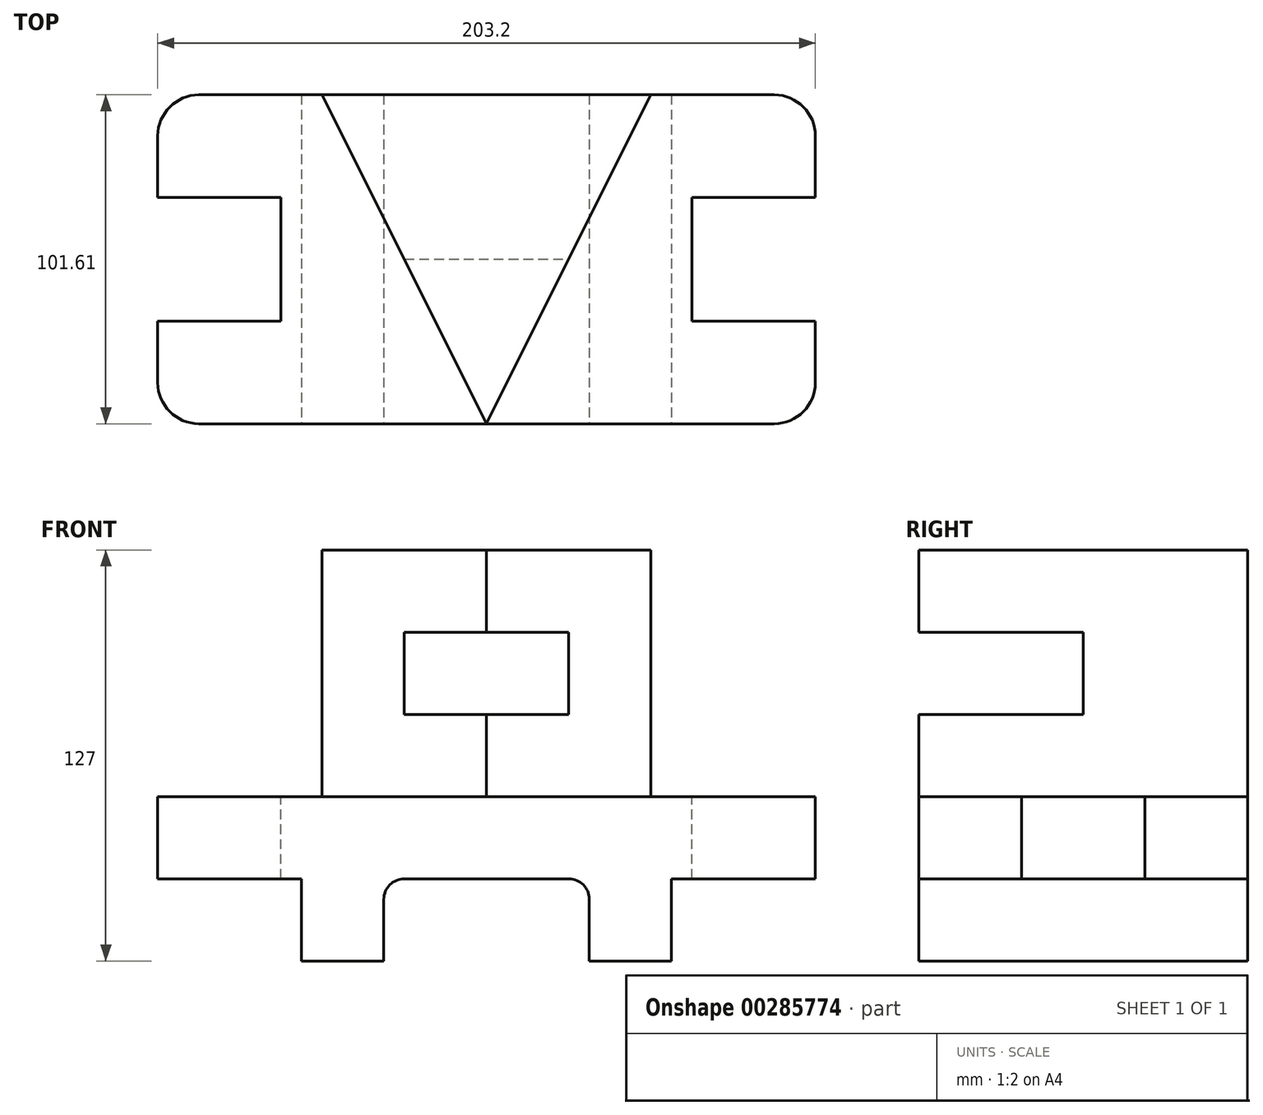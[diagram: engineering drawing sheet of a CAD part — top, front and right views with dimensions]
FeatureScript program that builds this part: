
annotation { "Feature Type Name" : "Feature", "Feature Type Description" : "" }
export const myFeature = defineFeature(function(context is Context, id is Id, definition is map)
    precondition{}
    {
        {
            var Q0;
            Q0=qCreatedBy(makeId("Top.planeOp"),FACE);
            var sketch = newSketch(context, id + "F0", { "sketchPlane" : qUnion([Q0])});
            skLineSegment(sketch, "E0", {"start": v(-50.8, 0) * mm, "end": v(50.8, 0) * mm});
            skLineSegment(sketch, "E1", {"start": v(0, 0) * mm, "end": v(0, -101.6) * mm, "construction": true});
            skLineSegment(sketch, "E2", {"start": v(50.8, 0) * mm, "end": v(0, -101.6) * mm});
            skLineSegment(sketch, "E3", {"start": v(-50.8, 0) * mm, "end": v(0, -101.6) * mm});
            skLineSegment(sketch, "E4", {"start": v(-25.4, -50.8) * mm, "end": v(25.4, -50.8) * mm});
            skSolve(sketch);
        }
        {
            var Q0;
            {var subQ3=sQuery(id+"F0.wireOp",EDGE,"E4");Q0=makeQuery(id+"F0.imprint","IMPRINT",FACE,{"disambiguationData":[TD([[makeQuery(id+"F0.imprint","IMPRINT",EDGE,{"derivedFrom":subQ3}),-1.0]])]});}
            var Q1;
            {var subQ0=sQuery(id+"F0.wireOp",EDGE,"E0");Q1=makeQuery(id+"F0.imprint","IMPRINT",FACE,{"disambiguationData":[TD([[makeQuery(id+"F0.imprint","IMPRINT",EDGE,{"derivedFrom":subQ0}),-1.0]])]});}
            extrude(context, id + "F1", {"entities" : qUnion([Q0, Q1]), "endBound" : BoundingType.SYMMETRIC, "depth" : 76.2 * mm});
        }
        {
            var Q0;
            {var subQ3=sQuery(id+"F0.wireOp",EDGE,"E4");Q0=makeQuery(id+"F0.imprint","IMPRINT",FACE,{"disambiguationData":[TD([[makeQuery(id+"F0.imprint","IMPRINT",EDGE,{"derivedFrom":subQ3}),-1.0]])]});}
            extrude(context, id + "F2", {"entities" : qUnion([Q0]), "operationType" : NewBodyOperationType.REMOVE, "endBound" : BoundingType.SYMMETRIC, "oppositeDirection" : true, "depth" : 25.4 * mm});
        }
        {
            var Q0;
            Q0=makeQuery(id+"F1.opExtrude","CAP_FACE",FACE,{"disambiguationData":[OSD([sQuery(id+"F0.wireOp",EDGE,"E0"),sQuery(id+"F0.wireOp",EDGE,"E2"),sQuery(id+"F0.wireOp",EDGE,"E3")])],"isStart":true});
            var sketch = newSketch(context, id + "F3", { "sketchPlane" : qUnion([Q0])});
            skLineSegment(sketch, "E5", {"start": v(-101.6, 0) * mm, "end": v(101.6, 0) * mm});
            skPoint(sketch, "E5.startSnap0", {"position": v(0, 0) * mm});
            skLineSegment(sketch, "E6", {"start": v(-101.6, 0) * mm, "end": v(-101.6, 101.6) * mm});
            skLineSegment(sketch, "E7", {"start": v(-101.6, 101.6) * mm, "end": v(101.6, 101.6) * mm});
            skLineSegment(sketch, "E8", {"start": v(101.6, 101.6) * mm, "end": v(101.6, 0) * mm});
            skArc(sketch, "E9", {"start": v(-88.9, 101.6) * mm, "mid": v(-97.88, 97.89) * mm, "end": v(-101.6, 88.9) * mm});
            skArc(sketch, "E10", {"start": v(101.6, 88.9) * mm, "mid": v(97.88, 97.89) * mm, "end": v(88.9, 101.6) * mm});
            skArc(sketch, "E11", {"start": v(88.9, 0) * mm, "mid": v(97.88, 3.72) * mm, "end": v(101.6, 12.7) * mm});
            skArc(sketch, "E12", {"start": v(-101.6, 12.7) * mm, "mid": v(-97.88, 3.72) * mm, "end": v(-88.9, 0) * mm});
            skLineSegment(sketch, "E13", {"start": v(-101.6, 31.75) * mm, "end": v(-63.5, 31.75) * mm});
            skLineSegment(sketch, "E14", {"start": v(-63.5, 31.75) * mm, "end": v(-63.5, 69.86) * mm});
            skLineSegment(sketch, "E15", {"start": v(-63.5, 69.86) * mm, "end": v(-101.6, 69.86) * mm});
            skLineSegment(sketch, "E16", {"start": v(101.6, 69.86) * mm, "end": v(63.5, 69.86) * mm});
            skLineSegment(sketch, "E17", {"start": v(63.5, 69.86) * mm, "end": v(63.5, 31.75) * mm});
            skLineSegment(sketch, "E18", {"start": v(63.5, 31.75) * mm, "end": v(101.6, 31.75) * mm});
            skSolve(sketch);
        }
        {
            var Q0;
            {var subQ2=makeQuery(id+"F1.opExtrude","CAP_EDGE",EDGE,{"disambiguationData":[OSD([sQuery(id+"F0.wireOp",EDGE,"E2")])],"isStart":true});Q0=makeQuery(id+"F3.imprint","IMPRINT",FACE,{"disambiguationData":[TD([[makeQuery(id+"F3.imprint","IMPRINT",EDGE,{"derivedFrom":subQ2}),1.0]])]});}
            var Q1;
            {var subQ1=sQuery(id+"F3.wireOp",EDGE,"E9");Q1=makeQuery(id+"F3.imprint","IMPRINT",FACE,{"disambiguationData":[TD([[makeQuery(id+"F3.imprint","IMPRINT",EDGE,{"derivedFrom":subQ1}),1.0]])]});}
            extrude(context, id + "F4", {"entities" : qUnion([Q0, Q1]), "operationType" : NewBodyOperationType.ADD, "depth" : 25.4 * mm});
        }
        {
            var Q0;
            Q0=makeQuery(id+"F4.opExtrude","SWEPT_FACE",FACE,{"disambiguationData":[OSD([sQuery(id+"F3.wireOp",EDGE,"E7")])]});
            var sketch = newSketch(context, id + "F5", { "sketchPlane" : qUnion([Q0])});
            skLineSegment(sketch, "E19", {"start": v(-57.15, -63.5) * mm, "end": v(-57.15, -88.9) * mm});
            skLineSegment(sketch, "E20", {"start": v(-57.15, -88.9) * mm, "end": v(-31.75, -88.9) * mm});
            skLineSegment(sketch, "E21", {"start": v(-31.75, -88.9) * mm, "end": v(-31.75, -63.5) * mm});
            skLineSegment(sketch, "E22", {"start": v(31.75, -63.5) * mm, "end": v(31.75, -88.9) * mm});
            skLineSegment(sketch, "E23", {"start": v(31.75, -88.9) * mm, "end": v(57.15, -88.9) * mm});
            skLineSegment(sketch, "E24", {"start": v(57.15, -88.9) * mm, "end": v(57.15, -63.5) * mm});
            skArc(sketch, "E25", {"start": v(-25.4, -63.5) * mm, "mid": v(-29.9, -65.36) * mm, "end": v(-31.75, -69.85) * mm});
            skArc(sketch, "E26", {"start": v(31.75, -69.85) * mm, "mid": v(29.9, -65.36) * mm, "end": v(25.4, -63.5) * mm});
            skPoint(sketch, "E27", {"position": v(31.75, -76.2) * mm});
            skSolve(sketch);
        }
        {
            var Q0;
            Q0 = qSketchRegion(id + "F5", true);
            var Q1;
            {var subQ5=sQuery(id+"F5.wireOp",EDGE,"E19");Q1=makeQuery(id+"F5.imprint","IMPRINT",FACE,{"disambiguationData":[TD([[makeQuery(id+"F5.imprint","IMPRINT",EDGE,{"derivedFrom":subQ5}),1.0]])]});}
            var Q2;
            {var subQ3=sQuery(id+"F5.wireOp",EDGE,"E25");Q2=makeQuery(id+"F5.imprint","IMPRINT",FACE,{"disambiguationData":[TD([[makeQuery(id+"F5.imprint","IMPRINT",EDGE,{"derivedFrom":subQ3}),-1.0]])]});}
            var Q3;
            {var subQ3=sQuery(id+"F5.wireOp",EDGE,"E26");Q3=makeQuery(id+"F5.imprint","IMPRINT",FACE,{"disambiguationData":[TD([[makeQuery(id+"F5.imprint","IMPRINT",EDGE,{"derivedFrom":subQ3}),-1.0]])]});}
            var Q4;
            {var subQ1=sQuery(id+"F5.wireOp",EDGE,"E23");Q4=makeQuery(id+"F5.imprint","IMPRINT",FACE,{"disambiguationData":[TD([[makeQuery(id+"F5.imprint","IMPRINT",EDGE,{"derivedFrom":subQ1}),1.0]])]});}
            var Q5;
            Q5=makeQuery(id+"F4.boolean.opBoolean","MERGE",FACE,{"derivedFrom":[makeQuery(id+"F1.opExtrude","SWEPT_FACE",FACE,{"disambiguationData":[OSD([sQuery(id+"F0.wireOp",EDGE,"E0")])]}),makeQuery(id+"F4.opExtrude","SWEPT_FACE",FACE,{"disambiguationData":[OSD([sQuery(id+"F3.wireOp",EDGE,"E5")])]})]});
            extrude(context, id + "F6", {"entities" : qUnion([Q0, Q1, Q2, Q3, Q4]), "operationType" : NewBodyOperationType.ADD, "endBound" : BoundingType.UP_TO_SURFACE, "oppositeDirection" : true, "endBoundEntityFace" : qUnion([Q5]), "depth" : 47.5 * mm});
        }
    });
